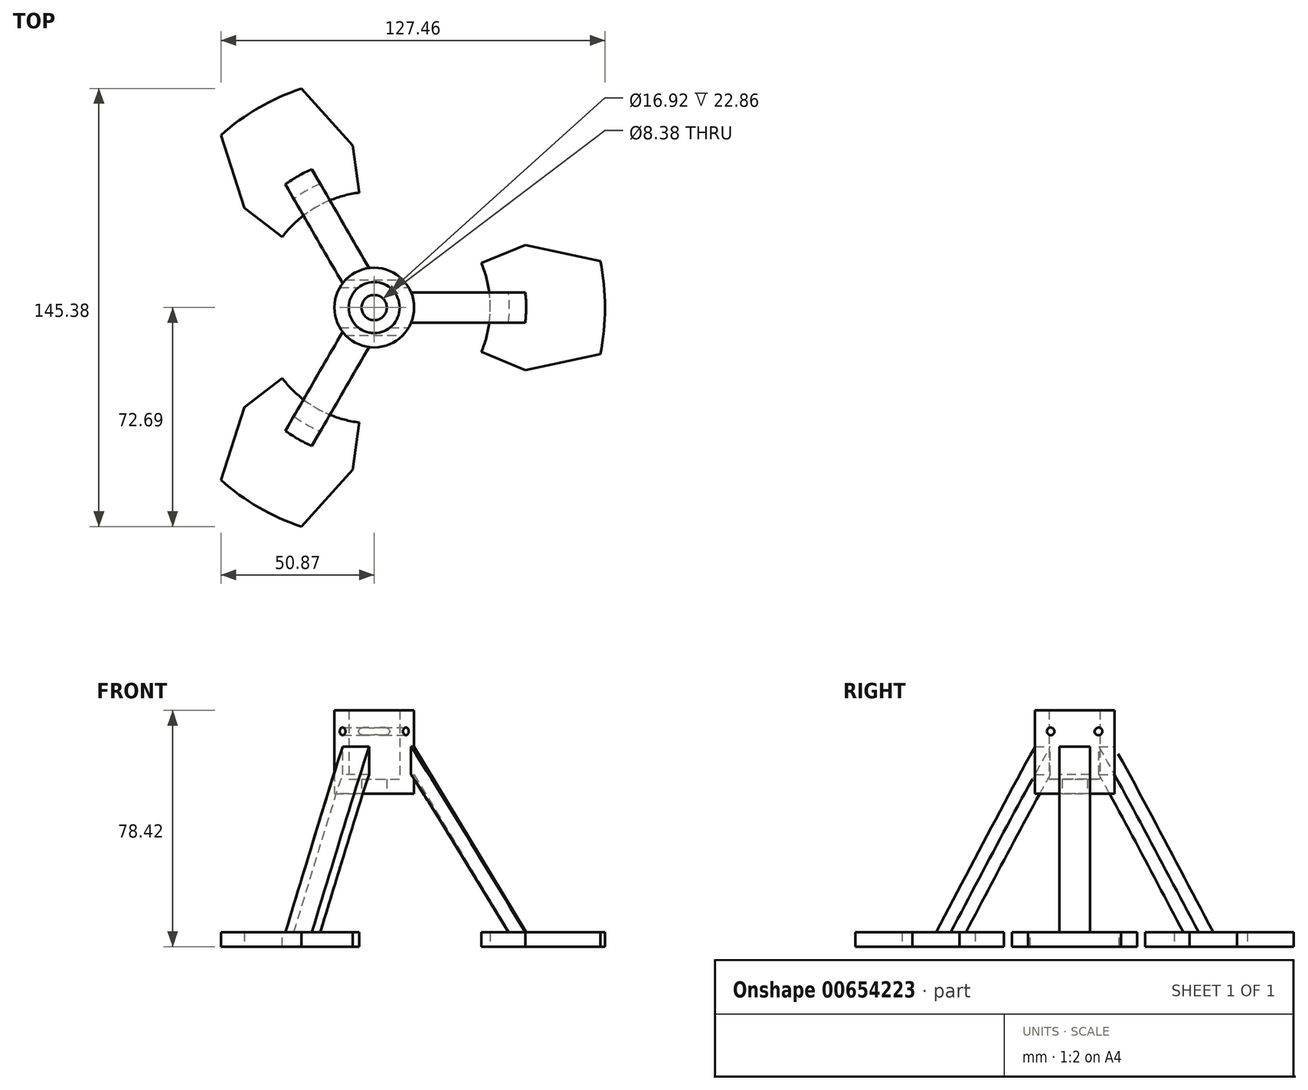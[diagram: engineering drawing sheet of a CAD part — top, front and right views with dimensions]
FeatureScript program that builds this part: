
annotation { "Feature Type Name" : "Feature", "Feature Type Description" : "" }
export const myFeature = defineFeature(function(context is Context, id is Id, definition is map)
    precondition{}
    {
        {
            var Q0;
            Q0=qCreatedBy(makeId("Front.planeOp"),FACE);
            var sketch = newSketch(context, id + "F0", { "sketchPlane" : qUnion([Q0])});
            skLineSegment(sketch, "E0.bottom", {"start": v(13.22, 78.42) * mm, "end": v(8.46, 78.42) * mm});
            skLineSegment(sketch, "E0.top", {"start": v(13.22, 50.8) * mm, "end": v(4.2, 50.8) * mm});
            skLineSegment(sketch, "E0.left", {"start": v(4.2, 55.56) * mm, "end": v(4.2, 50.8) * mm});
            skLineSegment(sketch, "E0.right", {"start": v(13.22, 78.42) * mm, "end": v(13.22, 50.8) * mm});
            skLineSegment(sketch, "E1", {"start": v(0, 49) * mm, "end": v(0, 103.42) * mm, "construction": true});
            skLineSegment(sketch, "E2", {"start": v(4.2, 55.56) * mm, "end": v(8.46, 55.56) * mm});
            skLineSegment(sketch, "E3", {"start": v(8.46, 55.56) * mm, "end": v(8.46, 78.42) * mm});
            skSolve(sketch);
        }
        {
            var Q0;
            Q0 = qSketchRegion(id + "F0", true);
            var Q1;
            Q1=sQuery(id+"F0.wireOp",EDGE,"E1");
            revolve(context, id + "F1", {"entities" : qUnion([Q0]), "axis" : qUnion([Q1]), "revolveType" : RevolveType.FULL});
        }
        {
            var Q0;
            Q0=qCreatedBy(makeId("Front.planeOp"),FACE);
            var sketch = newSketch(context, id + "F2", { "sketchPlane" : qUnion([Q0])});
            skLineSegment(sketch, "E4", {"start": v(13.22, 66.37) * mm, "end": v(50.4, 4.76) * mm});
            skLineSegment(sketch, "E5", {"start": v(76.6, 4.76) * mm, "end": v(76.6, 0) * mm});
            skLineSegment(sketch, "E6", {"start": v(76.6, 0) * mm, "end": v(38.5, 0) * mm});
            skLineSegment(sketch, "E7", {"start": v(38.5, 0) * mm, "end": v(38.5, 4.76) * mm});
            skLineSegment(sketch, "E8", {"start": v(44.84, 4.76) * mm, "end": v(13.22, 57.15) * mm});
            skLineSegment(sketch, "E9", {"start": v(44.84, 4.76) * mm, "end": v(38.5, 4.76) * mm});
            skLineSegment(sketch, "E10", {"start": v(13.22, 57.15) * mm, "end": v(13.22, 66.37) * mm});
            skLineSegment(sketch, "E11", {"start": v(50.4, 4.76) * mm, "end": v(76.6, 4.76) * mm});
            skPoint(sketch, "E12", {"position": v(63.5, 4.76) * mm});
            skSolve(sketch);
        }
        {
            var Q0;
            Q0 = qSketchRegion(id + "F2", true);
            var Q1;
            Q1=sQuery(id+"F0.wireOp",EDGE,"E1");
            revolve(context, id + "F3", {"entities" : qUnion([Q0]), "axis" : qUnion([Q1]), "revolveType" : RevolveType.SYMMETRIC, "angle" : 45 * degree});
        }
        {
            var Q0;
            Q0=qCreatedBy(makeId("Top.planeOp"),FACE);
            var sketch = newSketch(context, id + "F4", { "sketchPlane" : qUnion([Q0])});
            skLineSegment(sketch, "E13", {"start": v(12.21, 5.06) * mm, "end": v(63.5, 5.06) * mm});
            skLineSegment(sketch, "E14", {"start": v(63.5, 5.06) * mm, "end": v(63.5, -5.06) * mm});
            skLineSegment(sketch, "E15", {"start": v(63.5, -5.06) * mm, "end": v(12.21, -5.06) * mm});
            skLineSegment(sketch, "E16", {"start": v(12.21, -5.06) * mm, "end": v(12.21, -33.23) * mm});
            skLineSegment(sketch, "E17", {"start": v(12.21, -33.23) * mm, "end": v(78.25, -33.23) * mm});
            skLineSegment(sketch, "E18", {"start": v(78.25, -33.23) * mm, "end": v(78.25, 33.23) * mm});
            skLineSegment(sketch, "E19", {"start": v(78.25, 33.23) * mm, "end": v(12.21, 33.23) * mm});
            skLineSegment(sketch, "E20", {"start": v(12.21, 33.23) * mm, "end": v(12.21, 5.06) * mm});
            skSolve(sketch);
        }
        {
            var Q0;
            Q0 = qSketchRegion(id + "F4", true);
            extrude(context, id + "F5", {"entities" : qUnion([Q0]), "operationType" : NewBodyOperationType.REMOVE, "endBound" : BoundingType.THROUGH_ALL, "depth" : 25.4 * mm, "offsetDistance" : 25.4 * mm, "hasSecondDirection" : true, "secondDirectionOppositeDirection" : false, "secondDirectionDepth" : 4.76 * mm});
        }
        {
            var Q0;
            Q0=qCreatedBy(makeId("Top.planeOp"),FACE);
            var sketch = newSketch(context, id + "F6", { "sketchPlane" : qUnion([Q0])});
            skLineSegment(sketch, "E21", {"start": v(50.15, 20.77) * mm, "end": v(87.71, 12.7) * mm});
            skLineSegment(sketch, "E22", {"start": v(87.71, 12.7) * mm, "end": v(87.71, -12.7) * mm});
            skLineSegment(sketch, "E23", {"start": v(87.71, -12.7) * mm, "end": v(50.15, -20.77) * mm});
            skLineSegment(sketch, "E24", {"start": v(50.15, -20.77) * mm, "end": v(50.15, -36.6) * mm});
            skLineSegment(sketch, "E25", {"start": v(50.15, -36.6) * mm, "end": v(108.7, -36.6) * mm});
            skLineSegment(sketch, "E26", {"start": v(108.7, -36.6) * mm, "end": v(108.7, 31.76) * mm});
            skLineSegment(sketch, "E27", {"start": v(108.7, 31.76) * mm, "end": v(50.15, 31.76) * mm});
            skLineSegment(sketch, "E28", {"start": v(50.15, 31.76) * mm, "end": v(50.15, 20.77) * mm});
            skPoint(sketch, "E29", {"position": v(87.71, 0) * mm});
            skSolve(sketch);
        }
        {
            var Q0;
            Q0 = qSketchRegion(id + "F6", true);
            extrude(context, id + "F7", {"entities" : qUnion([Q0]), "operationType" : NewBodyOperationType.REMOVE, "endBound" : BoundingType.THROUGH_ALL, "depth" : 25.4 * mm, "offsetDistance" : 25.4 * mm});
        }
        {
            var Q0;
            Q0=makeQuery(id+"F3.opRevolve","SWEPT_BODY",BODY,{"disambiguationData":[OSD([sQuery(id+"F2.wireOp",EDGE,"E4"),sQuery(id+"F2.wireOp",EDGE,"E5"),sQuery(id+"F2.wireOp",EDGE,"E6"),sQuery(id+"F2.wireOp",EDGE,"E7"),sQuery(id+"F2.wireOp",EDGE,"E8"),sQuery(id+"F2.wireOp",EDGE,"E9"),sQuery(id+"F2.wireOp",EDGE,"R2gXq4uG-8riX-ghUQ-NOwH-sO4DdDGi5vsB"),sQuery(id+"F2.wireOp",EDGE,"JAp0I6LC-dbvt-FgDn-7RSW-C8dEAoY4syKf"),sQuery(id+"F2.wireOp",EDGE,"E10")])]});
            var Q1;
            Q1=sQuery(id+"F0.wireOp",EDGE,"E1");
            circularPattern(context, id + "F8", {"operationType" : NewBodyOperationType.ADD, "entities" : qUnion([Q0]), "axis" : qUnion([Q1]), "angle" : 360 * degree, "instanceCount" : 3, "equalSpace" : true});
        }
        {
            var Q0;
            Q0=qCreatedBy(makeId("Right.planeOp"),FACE);
            var sketch = newSketch(context, id + "F9", { "sketchPlane" : qUnion([Q0])});
            skCircle(sketch, "E30", {"center": v(-7.94, 71.44) * mm, "radius": 1.27 * mm});
            skCircle(sketch, "E31", {"center": v(7.94, 71.44) * mm, "radius": 1.27 * mm});
            skLineSegment(sketch, "E32", {"start": v(7.94, 71.44) * mm, "end": v(-7.94, 71.44) * mm, "construction": true});
            skPoint(sketch, "E33", {"position": v(0, 71.44) * mm});
            skSolve(sketch);
        }
        {
            var Q0;
            Q0 = qSketchRegion(id + "F9", true);
            extrude(context, id + "F10", {"entities" : qUnion([Q0]), "operationType" : NewBodyOperationType.REMOVE, "endBound" : BoundingType.THROUGH_ALL, "oppositeDirection" : true, "depth" : 25.4 * mm, "offsetDistance" : 25.4 * mm, "hasSecondDirection" : true, "secondDirectionBound" : SecondDirectionBoundingType.THROUGH_ALL, "secondDirectionOppositeDirection" : false, "secondDirectionDepth" : 25.4 * mm});
        }
    });
